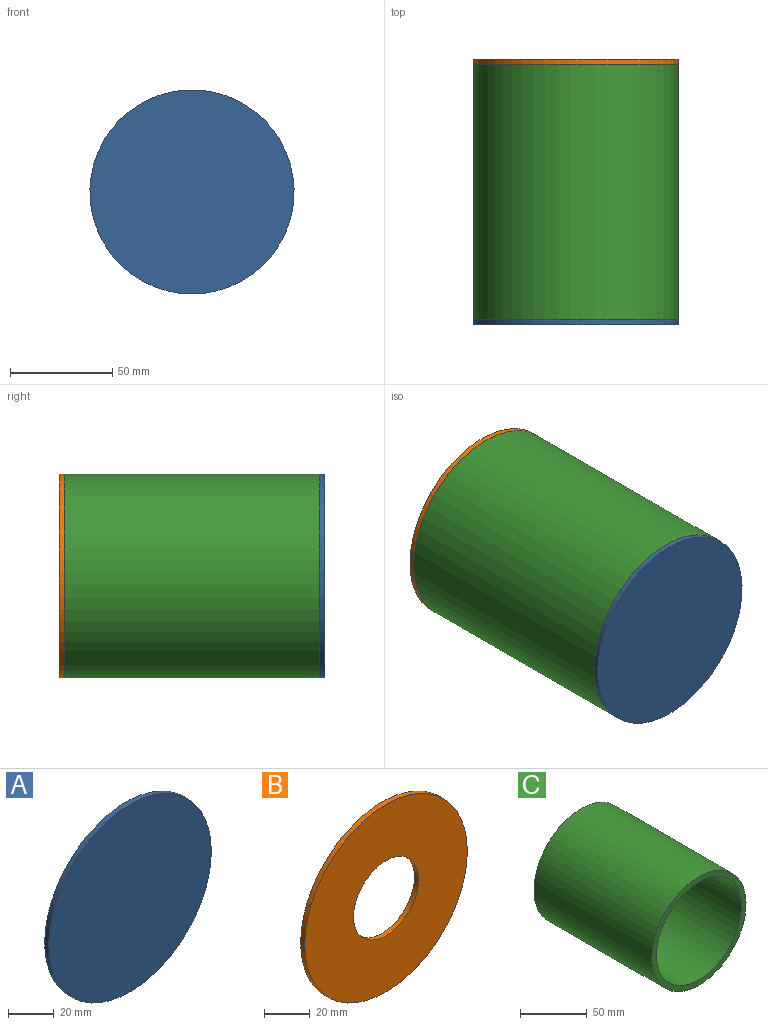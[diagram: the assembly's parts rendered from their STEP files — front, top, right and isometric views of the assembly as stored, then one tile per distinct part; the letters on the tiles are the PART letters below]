
ASSEMBLY  parts=3 mates=2
PART A: 3 faces, bbox 100x2.5x100 mm
  f0: cylinder r=50mm len=100mm, axis (0,1,0), area 785.4mm2, adj f1,f2
  f1: plane 100x100mm, normal (0,-1,0), area 7854mm2, adj f0
  f2: plane 100x100mm, normal (0,1,0), area 7854mm2, adj f0
PART B: 4 faces, bbox 100x2.5x100 mm
  f0: cylinder r=50mm len=100mm, axis (0,1,0), area 785.4mm2, adj f1,f2
  f1: plane 100x100mm, normal (0,-1,0), area 6597.3mm2, adj f0,f3
  f2: plane 100x100mm, normal (0,1,0), area 6597.3mm2, adj f0,f3
  f3: cylinder r=20mm len=40mm, axis (0,-1,0), area 314.2mm2, adj f1,f2
PART C: 4 faces, bbox 100x125x100 mm
  f0: cylinder r=45mm len=125mm, axis (0,1,0), area 35342.9mm2, adj f2,f3
  f1: cylinder r=50mm len=125mm, axis (0,1,0), area 39269.9mm2, adj f2,f3
  f2: plane 100x100mm, normal (0,-1,0), area 1492.3mm2, adj f0,f1
  f3: plane 100x100mm, normal (0,1,0), area 1492.3mm2, adj f0,f1
PLACE A t=(20.28,-111.3,195)mm
PLACE B t=(20.28,16.2,195)mm
PLACE C t=(20.28,13.7,195)mm
MATE fastened A.f0 <-> C.f1  axis (0,1,0) through (20.28,-111.3,195)mm
MATE fastened B.f0 <-> C.f0  axis (0,-1,0) through (20.28,13.7,195)mm
